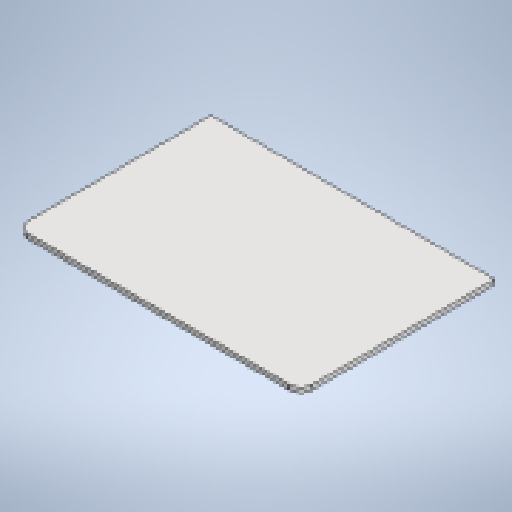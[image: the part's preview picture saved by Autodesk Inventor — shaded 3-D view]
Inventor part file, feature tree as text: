
AUTODESK INVENTOR PART (.ipt)
format: ipt  version: 2025 (Build 290162010, 162A)  size: 229,888 bytes
history: native  units: mm
features: sheet_metal_op x1, chamfer x1, sketch x1, other x1
ambient origin geometry x8: Origin, YZ Plane, XZ Plane, XY Plane, X Axis, Y Axis, Z Axis, Center Point
bodies: Solid1 (feature_tree)
feature tree (4):
  sheet_metal_op  "Face1"
  chamfer  "Corner Round2"
  sketch  "Sketch1"  dims[d0=120.0mm d1=82.0mm d2=2.0mm d4=4.75mm]
  other  "Plate1"
